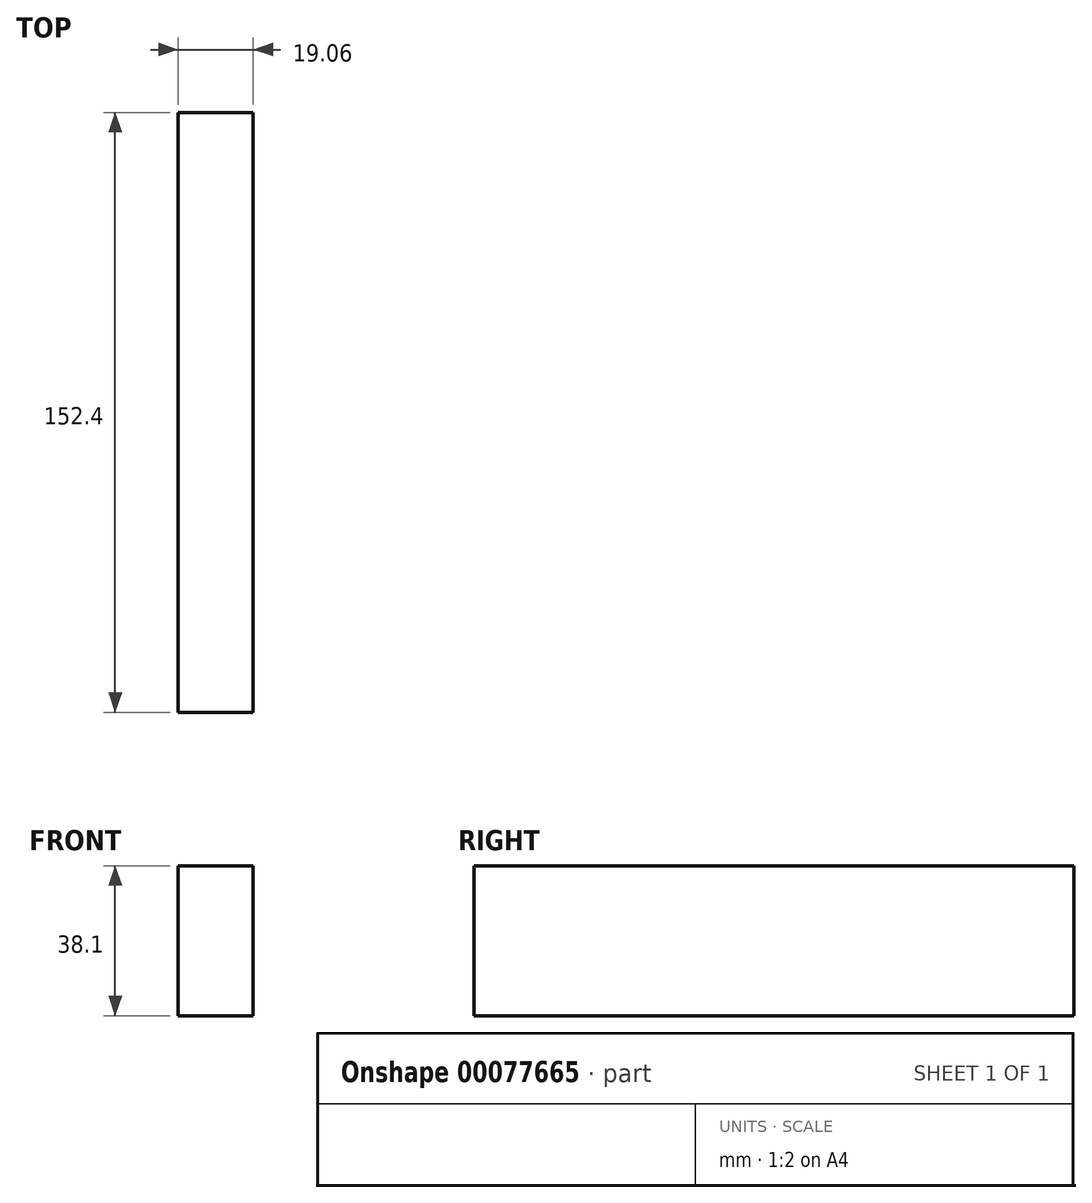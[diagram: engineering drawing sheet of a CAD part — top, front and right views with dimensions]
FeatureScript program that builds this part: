
annotation { "Feature Type Name" : "Feature", "Feature Type Description" : "" }
export const myFeature = defineFeature(function(context is Context, id is Id, definition is map)
    precondition{}
    {
        {
            var Q0;
            Q0=qCreatedBy(makeId("Front.planeOp"),FACE);
            var sketch = newSketch(context, id + "F0", { "sketchPlane" : qUnion([Q0])});
            skLineSegment(sketch, "E0", {"start": v(-9.53, 19.05) * mm, "end": v(9.53, 19.05) * mm});
            skLineSegment(sketch, "E1", {"start": v(9.53, 19.05) * mm, "end": v(9.53, -19.05) * mm});
            skLineSegment(sketch, "E2", {"start": v(9.53, -19.05) * mm, "end": v(-9.53, -19.05) * mm});
            skLineSegment(sketch, "E3", {"start": v(-9.53, -19.05) * mm, "end": v(-9.53, 19.05) * mm});
            skSolve(sketch);
        }
        {
            var Q0;
            Q0=makeQuery(id+"F0.imprint","IMPRINT",FACE,{"disambiguationData":[TD([[makeQuery(id+"F0.imprint","IMPRINT",EDGE,{"derivedFrom":sQuery(id+"F0.wireOp",EDGE,"E0")}),-1.0]])]});
            extrude(context, id + "F1", {"entities" : qUnion([Q0]), "depth" : 152.4 * mm});
        }
    });
